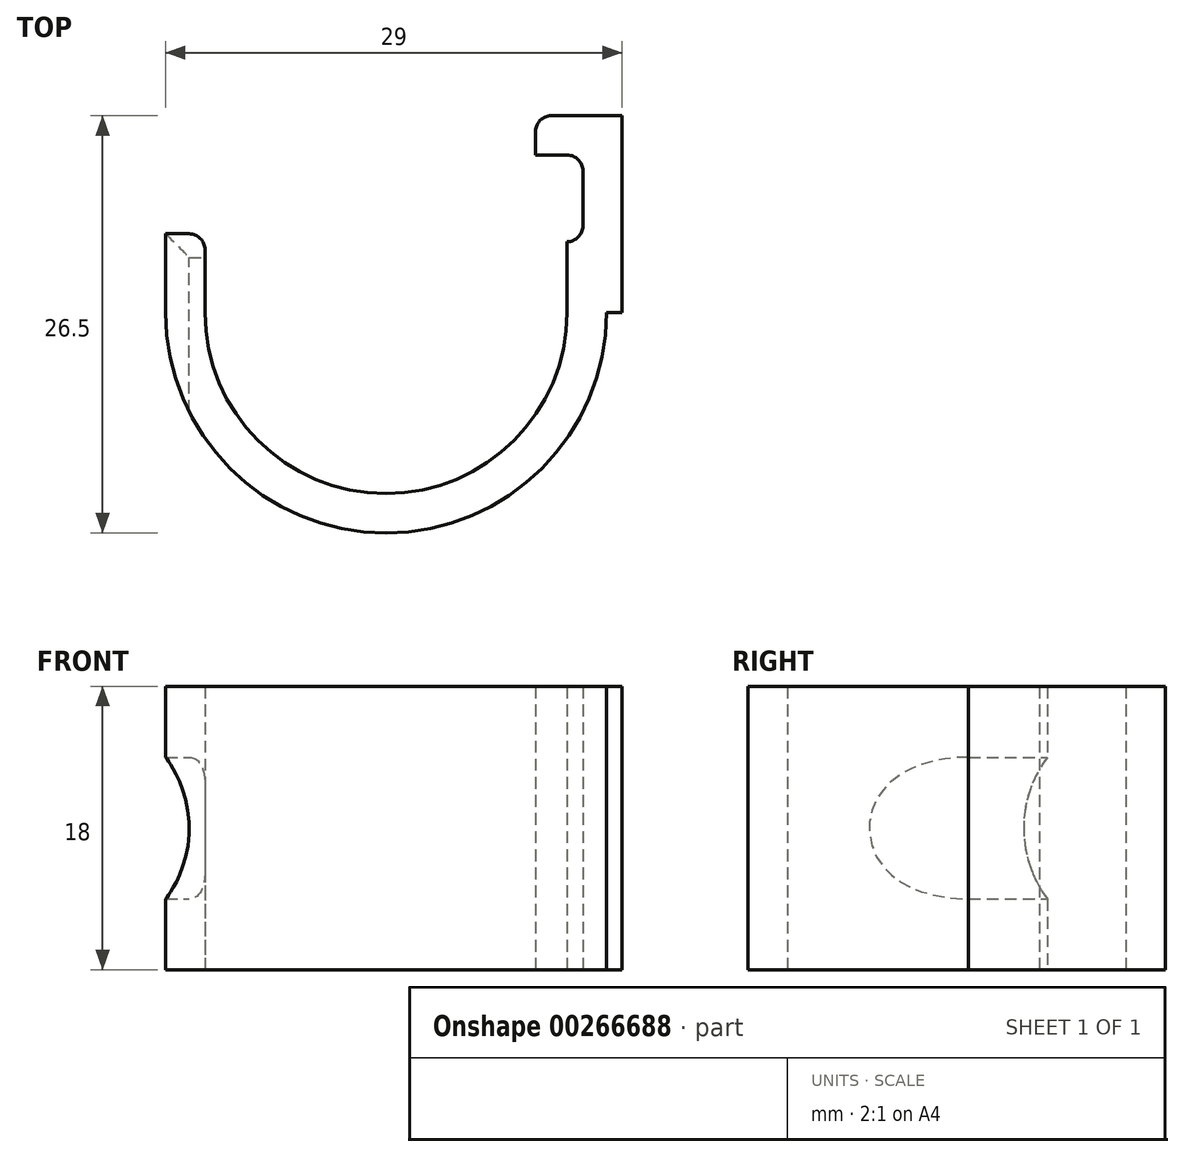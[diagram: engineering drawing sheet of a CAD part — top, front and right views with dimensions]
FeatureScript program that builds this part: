
annotation { "Feature Type Name" : "Feature", "Feature Type Description" : "" }
export const myFeature = defineFeature(function(context is Context, id is Id, definition is map)
    precondition{}
    {
        {
            var Q0;
            Q0=qCreatedBy(makeId("Top.planeOp"),FACE);
            var sketch = newSketch(context, id + "F0", { "sketchPlane" : qUnion([Q0])});
            skArc(sketch, "E0", {"start": v(-11.5, 0) * mm, "mid": v(0, -11.5) * mm, "end": v(11.5, 0) * mm});
            skArc(sketch, "E1", {"start": v(-14, 0) * mm, "mid": v(0, -14) * mm, "end": v(14, 0) * mm});
            skLineSegment(sketch, "E2", {"start": v(-14, 0) * mm, "end": v(-14, 5) * mm});
            skLineSegment(sketch, "E3", {"start": v(-14, 5) * mm, "end": v(-11.5, 5) * mm});
            skLineSegment(sketch, "E4", {"start": v(-11.5, 5) * mm, "end": v(-11.5, 0) * mm});
            skLineSegment(sketch, "E5", {"start": v(11.5, 0) * mm, "end": v(11.5, 4.5) * mm});
            skLineSegment(sketch, "E6", {"start": v(11.5, 4.5) * mm, "end": v(12.5, 4.5) * mm});
            skLineSegment(sketch, "E7", {"start": v(12.5, 4.5) * mm, "end": v(12.5, 10) * mm});
            skLineSegment(sketch, "E8", {"start": v(12.5, 10) * mm, "end": v(9.5, 10) * mm});
            skLineSegment(sketch, "E9", {"start": v(9.5, 10) * mm, "end": v(9.5, 12.5) * mm});
            skLineSegment(sketch, "E10", {"start": v(9.5, 12.5) * mm, "end": v(15, 12.5) * mm});
            skLineSegment(sketch, "E11", {"start": v(15, 12.5) * mm, "end": v(15, 0) * mm});
            skLineSegment(sketch, "E12", {"start": v(15, 0) * mm, "end": v(14, 0) * mm});
            skSolve(sketch);
        }
        {
            var Q0;
            Q0 = qSketchRegion(id + "F0", true);
            extrude(context, id + "F1", {"entities" : qUnion([Q0]), "depth" : 18 * mm});
        }
        {
            var Q0;
            Q0=makeQuery(id+"F1.opExtrude","SWEPT_FACE",FACE,{"disambiguationData":[OSD([sQuery(id+"F0.wireOp",EDGE,"E3")])]});
            var sketch = newSketch(context, id + "F2", { "sketchPlane" : qUnion([Q0])});
            skCircle(sketch, "E13", {"center": v(20, 9) * mm, "radius": 7.5 * mm});
            skPoint(sketch, "E14", {"position": v(12.5, 9) * mm});
            skPoint(sketch, "E14.positionSnap0", {"position": v(11.5, 9) * mm});
            skPoint(sketch, "E14.positionSnap1", {"position": v(12.75, 18) * mm});
            skSolve(sketch);
        }
        {
            var Q0;
            Q0 = qSketchRegion(id + "F2", true);
            extrude(context, id + "F3", {"entities" : qUnion([Q0]), "operationType" : NewBodyOperationType.REMOVE, "endBound" : BoundingType.THROUGH_ALL, "oppositeDirection" : true, "depth" : 25 * mm});
        }
        {
            var Q0;
            Q0=makeQuery(id+"F1.opExtrude","SWEPT_FACE",FACE,{"disambiguationData":[OSD([sQuery(id+"F0.wireOp",EDGE,"E4")])]});
            var sketch = newSketch(context, id + "F4", { "sketchPlane" : qUnion([Q0])});
            skPoint(sketch, "E15", {"position": v(3.5, 9) * mm});
            skPoint(sketch, "E15.positionSnap0", {"position": v(5, 9) * mm});
            skCircle(sketch, "E16", {"center": v(11, 9) * mm, "radius": 7.5 * mm});
            skSolve(sketch);
        }
        {
            var Q0;
            Q0 = qSketchRegion(id + "F4", true);
            extrude(context, id + "F5", {"entities" : qUnion([Q0]), "operationType" : NewBodyOperationType.REMOVE, "oppositeDirection" : true, "depth" : 25 * mm});
        }
        {
            var Q0;
            {var subQ0=sQuery(id+"F0.wireOp",EDGE,"E4");var subQ1=sQuery(id+"F0.wireOp",EDGE,"E3");Q0=makeQuery(id+"F5.boolean.opBoolean","SPLIT",EDGE,{"disambiguationData":[TD([makeQuery(id+"F1.opExtrude","CAP_FACE",FACE,{"disambiguationData":[OSD([sQuery(id+"F0.wireOp",EDGE,"E0"),sQuery(id+"F0.wireOp",EDGE,"E1"),sQuery(id+"F0.wireOp",EDGE,"E2"),subQ1,subQ0,sQuery(id+"F0.wireOp",EDGE,"E5"),sQuery(id+"F0.wireOp",EDGE,"E6"),sQuery(id+"F0.wireOp",EDGE,"E7"),sQuery(id+"F0.wireOp",EDGE,"E8"),sQuery(id+"F0.wireOp",EDGE,"E9"),sQuery(id+"F0.wireOp",EDGE,"E10"),sQuery(id+"F0.wireOp",EDGE,"E11"),sQuery(id+"F0.wireOp",EDGE,"E12")])],"isStart":false})])],"derivedFrom":makeQuery(id+"F1.opExtrude","SWEPT_EDGE",EDGE,{"disambiguationData":[OSD([subQ1,subQ0])]})});}
            var Q1;
            {var subQ0=sQuery(id+"F0.wireOp",EDGE,"E4");var subQ1=sQuery(id+"F0.wireOp",EDGE,"E3");Q1=makeQuery(id+"F5.boolean.opBoolean","SPLIT",EDGE,{"disambiguationData":[TD([makeQuery(id+"F1.opExtrude","CAP_FACE",FACE,{"disambiguationData":[OSD([sQuery(id+"F0.wireOp",EDGE,"E0"),sQuery(id+"F0.wireOp",EDGE,"E1"),sQuery(id+"F0.wireOp",EDGE,"E2"),subQ1,subQ0,sQuery(id+"F0.wireOp",EDGE,"E5"),sQuery(id+"F0.wireOp",EDGE,"E6"),sQuery(id+"F0.wireOp",EDGE,"E7"),sQuery(id+"F0.wireOp",EDGE,"E8"),sQuery(id+"F0.wireOp",EDGE,"E9"),sQuery(id+"F0.wireOp",EDGE,"E10"),sQuery(id+"F0.wireOp",EDGE,"E11"),sQuery(id+"F0.wireOp",EDGE,"E12")])],"isStart":true})])],"derivedFrom":makeQuery(id+"F1.opExtrude","SWEPT_EDGE",EDGE,{"disambiguationData":[OSD([subQ1,subQ0])]})});}
            var Q2;
            Q2=makeQuery(id+"F1.opExtrude","SWEPT_EDGE",EDGE,{"disambiguationData":[OSD([sQuery(id+"F0.wireOp",EDGE,"E6"),sQuery(id+"F0.wireOp",EDGE,"E7")])]});
            var Q3;
            Q3=makeQuery(id+"F1.opExtrude","SWEPT_EDGE",EDGE,{"disambiguationData":[OSD([sQuery(id+"F0.wireOp",EDGE,"E7"),sQuery(id+"F0.wireOp",EDGE,"E8")])]});
            var Q4;
            Q4=makeQuery(id+"F1.opExtrude","SWEPT_EDGE",EDGE,{"disambiguationData":[OSD([sQuery(id+"F0.wireOp",EDGE,"E9"),sQuery(id+"F0.wireOp",EDGE,"E10")])]});
            fillet(context, id + "F6", {"entities" : qUnion([Q0, Q1, Q2, Q3, Q4]), "radius" : 1 * mm, "tangentPropagation" : true, "allowEdgeOverflow" : false});
        }
    });
